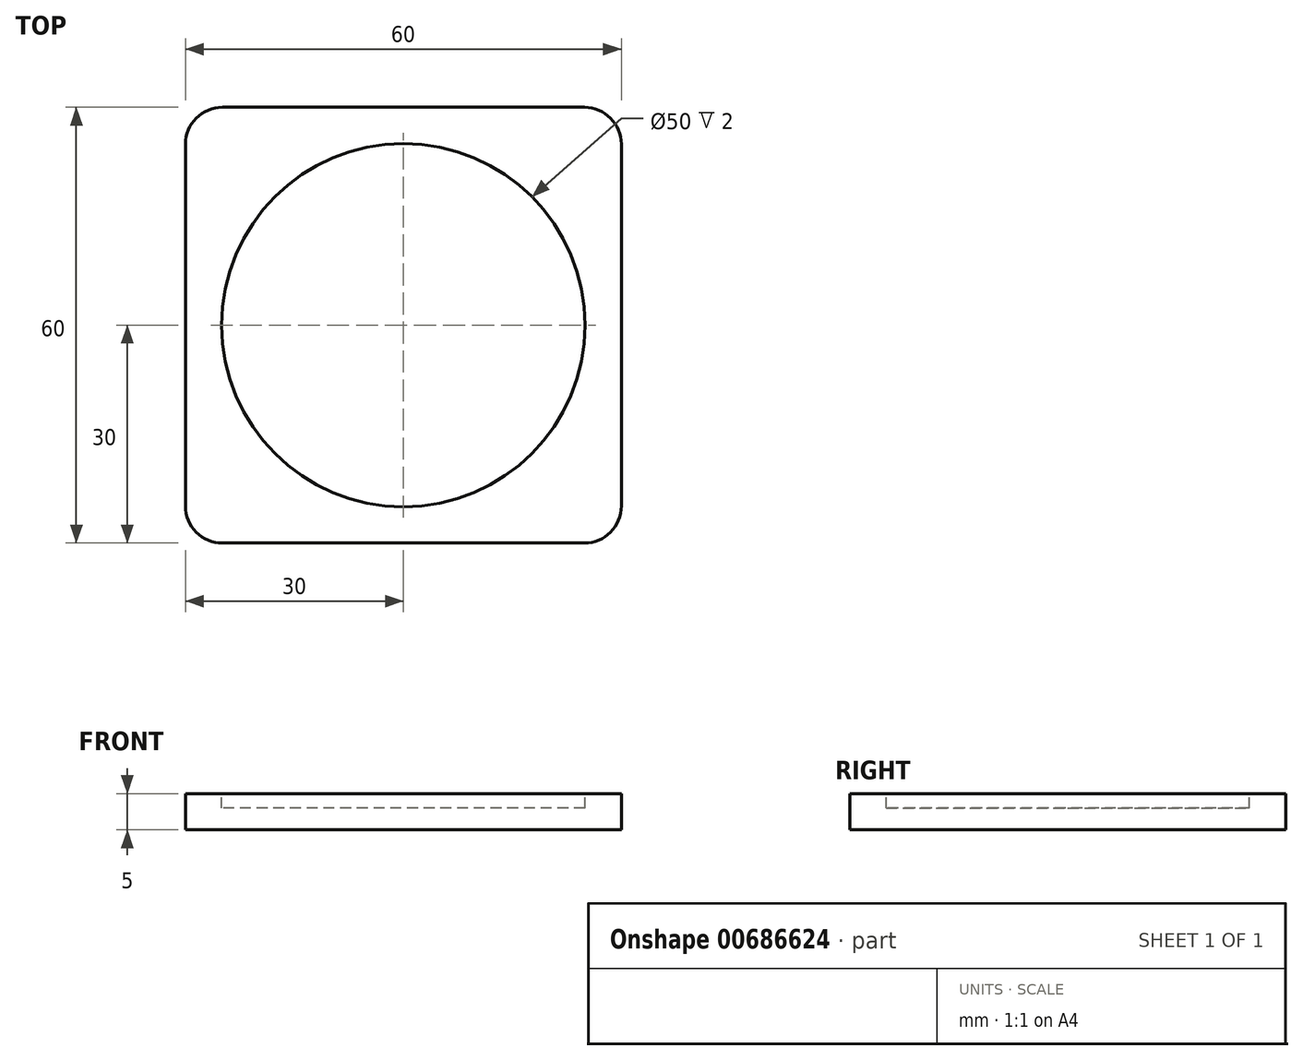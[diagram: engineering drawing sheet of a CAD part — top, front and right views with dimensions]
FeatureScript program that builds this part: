
annotation { "Feature Type Name" : "Feature", "Feature Type Description" : "" }
export const myFeature = defineFeature(function(context is Context, id is Id, definition is map)
    precondition{}
    {
        {
            var Q0;
            Q0=qCreatedBy(makeId("Top.planeOp"),FACE);
            var sketch = newSketch(context, id + "F0", { "sketchPlane" : qUnion([Q0])});
            skLineSegment(sketch, "E0.bottom", {"start": v(30, 30) * mm, "end": v(-30, 30) * mm});
            skLineSegment(sketch, "E0.top", {"start": v(30, -30) * mm, "end": v(-30, -30) * mm});
            skLineSegment(sketch, "E0.left", {"start": v(30, 30) * mm, "end": v(30, -30) * mm});
            skLineSegment(sketch, "E0.right", {"start": v(-30, 30) * mm, "end": v(-30, -30) * mm});
            skPoint(sketch, "E0.middle", {"position": v(0, 0) * mm});
            skSolve(sketch);
        }
        {
            var Q0;
            Q0=makeQuery(id+"F0.imprint","IMPRINT",FACE,{"disambiguationData":[TD([[makeQuery(id+"F0.imprint","IMPRINT",EDGE,{"derivedFrom":sQuery(id+"F0.wireOp",EDGE,"E0.bottom")}),1.0]])]});
            extrude(context, id + "F1", {"entities" : qUnion([Q0]), "depth" : 5 * mm, "offsetDistance" : 25.4 * mm});
        }
        {
            var Q0;
            Q0=makeQuery(id+"F1.opExtrude","CAP_FACE",FACE,{"disambiguationData":[OSD([sQuery(id+"F0.wireOp",EDGE,"E0.bottom"),sQuery(id+"F0.wireOp",EDGE,"E0.top"),sQuery(id+"F0.wireOp",EDGE,"E0.left"),sQuery(id+"F0.wireOp",EDGE,"E0.right")])],"isStart":false});
            var sketch = newSketch(context, id + "F2", { "sketchPlane" : qUnion([Q0])});
            skCircle(sketch, "E1", {"center": v(0, 0) * mm, "radius": 25 * mm});
            skSolve(sketch);
        }
        {
            var Q0;
            Q0=makeQuery(id+"F2.imprint","IMPRINT",FACE,{"disambiguationData":[TD([[makeQuery(id+"F2.imprint","IMPRINT",EDGE,{"derivedFrom":sQuery(id+"F2.wireOp",EDGE,"E1")}),1.0]])]});
            extrude(context, id + "F3", {"entities" : qUnion([Q0]), "operationType" : NewBodyOperationType.REMOVE, "oppositeDirection" : true, "depth" : 2 * mm, "offsetDistance" : 25.4 * mm});
        }
        {
            var Q0;
            Q0=makeQuery(id+"F1.opExtrude","SWEPT_EDGE",EDGE,{"disambiguationData":[OSD([sQuery(id+"F0.wireOp",EDGE,"E0.bottom"),sQuery(id+"F0.wireOp",EDGE,"E0.right")])]});
            var Q1;
            Q1=makeQuery(id+"F1.opExtrude","SWEPT_EDGE",EDGE,{"disambiguationData":[OSD([sQuery(id+"F0.wireOp",EDGE,"E0.bottom"),sQuery(id+"F0.wireOp",EDGE,"E0.left")])]});
            var Q2;
            Q2=makeQuery(id+"F1.opExtrude","SWEPT_EDGE",EDGE,{"disambiguationData":[OSD([sQuery(id+"F0.wireOp",EDGE,"E0.top"),sQuery(id+"F0.wireOp",EDGE,"E0.left")])]});
            var Q3;
            Q3=makeQuery(id+"F1.opExtrude","SWEPT_EDGE",EDGE,{"disambiguationData":[OSD([sQuery(id+"F0.wireOp",EDGE,"E0.top"),sQuery(id+"F0.wireOp",EDGE,"E0.right")])]});
            fillet(context, id + "F4", {"entities" : qUnion([Q0, Q1, Q2, Q3]), "radius" : 5.08 * mm, "tangentPropagation" : true, "allowEdgeOverflow" : false});
        }
    });
